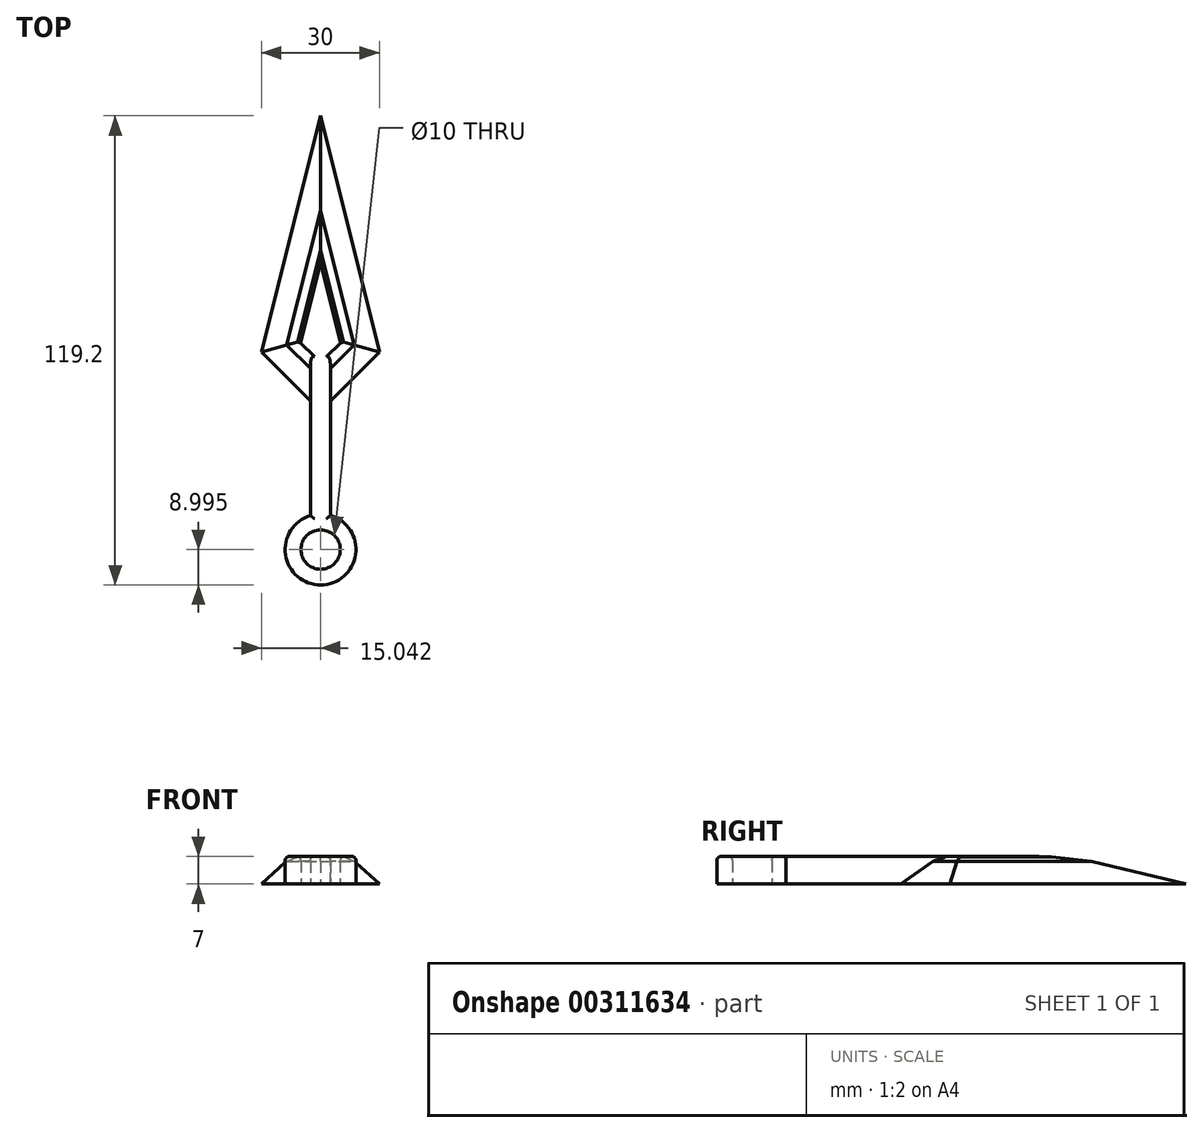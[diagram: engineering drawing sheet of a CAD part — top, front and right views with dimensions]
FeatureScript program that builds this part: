
annotation { "Feature Type Name" : "Feature", "Feature Type Description" : "" }
export const myFeature = defineFeature(function(context is Context, id is Id, definition is map)
    precondition{}
    {
        {
            var Q0;
            Q0=qCreatedBy(makeId("Top.planeOp"),FACE);
            var sketch = newSketch(context, id + "F0", { "sketchPlane" : qUnion([Q0])});
            skLineSegment(sketch, "E0", {"start": v(0, 0) * mm, "end": v(0, 60) * mm, "construction": true});
            skLineSegment(sketch, "E1", {"start": v(0, 0) * mm, "end": v(0, -15) * mm, "construction": true});
            skLineSegment(sketch, "E2", {"start": v(0, -15) * mm, "end": v(0, -45.92) * mm, "construction": true});
            skLineSegment(sketch, "E3", {"start": v(-15, 0) * mm, "end": v(0, 0) * mm, "construction": true});
            skLineSegment(sketch, "E4", {"start": v(0, 0) * mm, "end": v(15, 0) * mm, "construction": true});
            skLineSegment(sketch, "E5", {"start": v(0, 60) * mm, "end": v(-15, 0) * mm});
            skLineSegment(sketch, "E6", {"start": v(-15, 0) * mm, "end": v(0, -15) * mm});
            skLineSegment(sketch, "E7", {"start": v(0, -15) * mm, "end": v(15, 0) * mm});
            skLineSegment(sketch, "E8", {"start": v(15, 0) * mm, "end": v(0, 60) * mm});
            skLineSegment(sketch, "E9", {"start": v(-2.54, -12.46) * mm, "end": v(-2.54, -45.92) * mm});
            skLineSegment(sketch, "E10.MirrorCS", {"start": v(2.54, -12.46) * mm, "end": v(2.54, -45.92) * mm});
            skCircle(sketch, "E11", {"center": v(0.04, -50.2) * mm, "radius": 9 * mm});
            skPoint(sketch, "E11.first.point", {"position": v(0, -59.2) * mm});
            skPoint(sketch, "E11.second.point", {"position": v(0, -41.2) * mm});
            skPoint(sketch, "E11.third.point", {"position": v(8.9, -51.77) * mm});
            skCircle(sketch, "E12", {"center": v(0.04, -50.2) * mm, "radius": 5 * mm});
            skSolve(sketch);
        }
        {
            var Q0;
            {var subQ5=sQuery(id+"F0.wireOp",EDGE,"E5");Q0=makeQuery(id+"F0.imprint","IMPRINT",FACE,{"disambiguationData":[TD([[makeQuery(id+"F0.imprint","IMPRINT",EDGE,{"derivedFrom":subQ5}),1.0]])]});}
            var Q1;
            {var subQ0=sQuery(id+"F0.wireOp",EDGE,"E12");var subQ1=sQuery(id+"F0.wireOp",EDGE,"E9");var subQ2=makeQuery(id+"F0.imprint","INTERSECT",VERTEX,{"derivedFrom":[subQ1,subQ0]});Q1=makeQuery(id+"F0.imprint","IMPRINT",FACE,{"disambiguationData":[TD([[makeQuery(id+"F0.imprint","IMPRINT",EDGE,{"disambiguationData":[TD([[subQ2,1.0]])],"derivedFrom":subQ1}),1.0]])]});}
            var Q2;
            {var subQ0=sQuery(id+"F0.wireOp",EDGE,"E12");var subQ1=sQuery(id+"F0.wireOp",EDGE,"E9");var subQ2=makeQuery(id+"F0.imprint","INTERSECT",VERTEX,{"derivedFrom":[subQ1,subQ0]});Q2=makeQuery(id+"F0.imprint","IMPRINT",FACE,{"disambiguationData":[TD([[makeQuery(id+"F0.imprint","IMPRINT",EDGE,{"disambiguationData":[TD([[subQ2,1.0]])],"derivedFrom":subQ1}),-1.0]])]});}
            var Q3;
            {var subQ1=sQuery(id+"F0.wireOp",EDGE,"E6");var subQ6=sQuery(id+"F0.wireOp",EDGE,"E7");var subQ9=makeQuery(id+"F0.imprint","INTERSECT",VERTEX,{"derivedFrom":[subQ1,subQ6]});Q3=makeQuery(id+"F0.imprint","IMPRINT",FACE,{"disambiguationData":[TD([[makeQuery(id+"F0.imprint","IMPRINT",EDGE,{"disambiguationData":[TD([[subQ9,1.0]])],"derivedFrom":subQ1}),-1.0]])]});}
            extrude(context, id + "F1", {"entities" : qUnion([Q0, Q1, Q2, Q3]), "depth" : 7 * mm});
        }
        {
            var Q0;
            Q0=makeQuery(id+"F1.opExtrude","CAP_EDGE",EDGE,{"disambiguationData":[OSD([sQuery(id+"F0.wireOp",EDGE,"E5")])],"isStart":false});
            var Q1;
            Q1=makeQuery(id+"F1.opExtrude","CAP_EDGE",EDGE,{"disambiguationData":[OSD([sQuery(id+"F0.wireOp",EDGE,"E8")])],"isStart":false});
            var Q2;
            Q2=makeQuery(id+"F1.opExtrude","CAP_EDGE",EDGE,{"disambiguationData":[OSD([sQuery(id+"F0.wireOp",EDGE,"E6")])],"isStart":false});
            var Q3;
            Q3=makeQuery(id+"F1.opExtrude","CAP_EDGE",EDGE,{"disambiguationData":[OSD([sQuery(id+"F0.wireOp",EDGE,"E7")])],"isStart":false});
            chamfer(context, id + "F2", {"entities" : qUnion([Q0, Q1, Q2, Q3]), "width" : 7 * mm, "tangentPropagation" : true});
        }
        {
            var Q0;
            {var subQ0=sQuery(id+"F0.wireOp",EDGE,"E5");Q0=makeQuery(id+"F2.opChamfer","BLEND_EDGE",EDGE,{"blendedFrom":[makeQuery(id+"F1.opExtrude","CAP_EDGE",EDGE,{"disambiguationData":[OSD([subQ0])],"isStart":false}),makeQuery(id+"F1.opExtrude","CAP_FACE",FACE,{"disambiguationData":[OSD([subQ0,sQuery(id+"F0.wireOp",EDGE,"E6"),sQuery(id+"F0.wireOp",EDGE,"E7"),sQuery(id+"F0.wireOp",EDGE,"E8"),sQuery(id+"F0.wireOp",EDGE,"E9"),sQuery(id+"F0.wireOp",EDGE,"E10.MirrorCS"),sQuery(id+"F0.wireOp",EDGE,"E11"),sQuery(id+"F0.wireOp",EDGE,"E12")])],"isStart":false})],"blendedInto":[makeQuery(id+"F1.opExtrude","CAP_FACE",FACE,{"disambiguationData":[OSD([subQ0,sQuery(id+"F0.wireOp",EDGE,"E6"),sQuery(id+"F0.wireOp",EDGE,"E7"),sQuery(id+"F0.wireOp",EDGE,"E8"),sQuery(id+"F0.wireOp",EDGE,"E9"),sQuery(id+"F0.wireOp",EDGE,"E10.MirrorCS"),sQuery(id+"F0.wireOp",EDGE,"E11"),sQuery(id+"F0.wireOp",EDGE,"E12")])],"isStart":false})]});}
            var Q1;
            {var subQ0=sQuery(id+"F0.wireOp",EDGE,"E8");Q1=makeQuery(id+"F2.opChamfer","BLEND_EDGE",EDGE,{"blendedFrom":[makeQuery(id+"F1.opExtrude","CAP_EDGE",EDGE,{"disambiguationData":[OSD([subQ0])],"isStart":false}),makeQuery(id+"F1.opExtrude","CAP_FACE",FACE,{"disambiguationData":[OSD([sQuery(id+"F0.wireOp",EDGE,"E5"),sQuery(id+"F0.wireOp",EDGE,"E6"),sQuery(id+"F0.wireOp",EDGE,"E7"),subQ0,sQuery(id+"F0.wireOp",EDGE,"E9"),sQuery(id+"F0.wireOp",EDGE,"E10.MirrorCS"),sQuery(id+"F0.wireOp",EDGE,"E11"),sQuery(id+"F0.wireOp",EDGE,"E12")])],"isStart":false})],"blendedInto":[makeQuery(id+"F1.opExtrude","CAP_FACE",FACE,{"disambiguationData":[OSD([sQuery(id+"F0.wireOp",EDGE,"E5"),sQuery(id+"F0.wireOp",EDGE,"E6"),sQuery(id+"F0.wireOp",EDGE,"E7"),subQ0,sQuery(id+"F0.wireOp",EDGE,"E9"),sQuery(id+"F0.wireOp",EDGE,"E10.MirrorCS"),sQuery(id+"F0.wireOp",EDGE,"E11"),sQuery(id+"F0.wireOp",EDGE,"E12")])],"isStart":false})]});}
            var Q2;
            {var subQ0=sQuery(id+"F0.wireOp",EDGE,"E6");Q2=makeQuery(id+"F2.opChamfer","BLEND_EDGE",EDGE,{"blendedFrom":[makeQuery(id+"F1.opExtrude","CAP_EDGE",EDGE,{"disambiguationData":[OSD([subQ0])],"isStart":false}),makeQuery(id+"F1.opExtrude","CAP_FACE",FACE,{"disambiguationData":[OSD([sQuery(id+"F0.wireOp",EDGE,"E5"),subQ0,sQuery(id+"F0.wireOp",EDGE,"E7"),sQuery(id+"F0.wireOp",EDGE,"E8"),sQuery(id+"F0.wireOp",EDGE,"E9"),sQuery(id+"F0.wireOp",EDGE,"E10.MirrorCS"),sQuery(id+"F0.wireOp",EDGE,"E11"),sQuery(id+"F0.wireOp",EDGE,"E12")])],"isStart":false})],"blendedInto":[makeQuery(id+"F1.opExtrude","CAP_FACE",FACE,{"disambiguationData":[OSD([sQuery(id+"F0.wireOp",EDGE,"E5"),subQ0,sQuery(id+"F0.wireOp",EDGE,"E7"),sQuery(id+"F0.wireOp",EDGE,"E8"),sQuery(id+"F0.wireOp",EDGE,"E9"),sQuery(id+"F0.wireOp",EDGE,"E10.MirrorCS"),sQuery(id+"F0.wireOp",EDGE,"E11"),sQuery(id+"F0.wireOp",EDGE,"E12")])],"isStart":false})]});}
            var Q3;
            {var subQ0=sQuery(id+"F0.wireOp",EDGE,"E7");Q3=makeQuery(id+"F2.opChamfer","BLEND_EDGE",EDGE,{"blendedFrom":[makeQuery(id+"F1.opExtrude","CAP_EDGE",EDGE,{"disambiguationData":[OSD([subQ0])],"isStart":false}),makeQuery(id+"F1.opExtrude","CAP_FACE",FACE,{"disambiguationData":[OSD([sQuery(id+"F0.wireOp",EDGE,"E5"),sQuery(id+"F0.wireOp",EDGE,"E6"),subQ0,sQuery(id+"F0.wireOp",EDGE,"E8"),sQuery(id+"F0.wireOp",EDGE,"E9"),sQuery(id+"F0.wireOp",EDGE,"E10.MirrorCS"),sQuery(id+"F0.wireOp",EDGE,"E11"),sQuery(id+"F0.wireOp",EDGE,"E12")])],"isStart":false})],"blendedInto":[makeQuery(id+"F1.opExtrude","CAP_FACE",FACE,{"disambiguationData":[OSD([sQuery(id+"F0.wireOp",EDGE,"E5"),sQuery(id+"F0.wireOp",EDGE,"E6"),subQ0,sQuery(id+"F0.wireOp",EDGE,"E8"),sQuery(id+"F0.wireOp",EDGE,"E9"),sQuery(id+"F0.wireOp",EDGE,"E10.MirrorCS"),sQuery(id+"F0.wireOp",EDGE,"E11"),sQuery(id+"F0.wireOp",EDGE,"E12")])],"isStart":false})]});}
            chamfer(context, id + "F3", {"entities" : qUnion([Q0, Q1, Q2, Q3]), "width" : 4 * mm, "tangentPropagation" : true});
        }
        {
            var Q0;
            {var subQ0=sQuery(id+"F0.wireOp",EDGE,"E5");var subQ1=makeQuery(id+"F1.opExtrude","CAP_FACE",FACE,{"disambiguationData":[OSD([subQ0,sQuery(id+"F0.wireOp",EDGE,"E6"),sQuery(id+"F0.wireOp",EDGE,"E7"),sQuery(id+"F0.wireOp",EDGE,"E8"),sQuery(id+"F0.wireOp",EDGE,"E9"),sQuery(id+"F0.wireOp",EDGE,"E10.MirrorCS"),sQuery(id+"F0.wireOp",EDGE,"E11"),sQuery(id+"F0.wireOp",EDGE,"E12")])],"isStart":false});Q0=makeQuery(id+"F3.opChamfer","BLEND_EDGE",EDGE,{"blendedFrom":[makeQuery(id+"F2.opChamfer","BLEND_EDGE",EDGE,{"blendedFrom":[makeQuery(id+"F1.opExtrude","CAP_EDGE",EDGE,{"disambiguationData":[OSD([subQ0])],"isStart":false}),subQ1],"blendedInto":[subQ1]}),subQ1],"blendedInto":[subQ1]});}
            var Q1;
            {var subQ0=sQuery(id+"F0.wireOp",EDGE,"E8");var subQ1=makeQuery(id+"F1.opExtrude","CAP_FACE",FACE,{"disambiguationData":[OSD([sQuery(id+"F0.wireOp",EDGE,"E5"),sQuery(id+"F0.wireOp",EDGE,"E6"),sQuery(id+"F0.wireOp",EDGE,"E7"),subQ0,sQuery(id+"F0.wireOp",EDGE,"E9"),sQuery(id+"F0.wireOp",EDGE,"E10.MirrorCS"),sQuery(id+"F0.wireOp",EDGE,"E11"),sQuery(id+"F0.wireOp",EDGE,"E12")])],"isStart":false});Q1=makeQuery(id+"F3.opChamfer","BLEND_EDGE",EDGE,{"blendedFrom":[makeQuery(id+"F2.opChamfer","BLEND_EDGE",EDGE,{"blendedFrom":[makeQuery(id+"F1.opExtrude","CAP_EDGE",EDGE,{"disambiguationData":[OSD([subQ0])],"isStart":false}),subQ1],"blendedInto":[subQ1]}),subQ1],"blendedInto":[subQ1]});}
            chamfer(context, id + "F4", {"entities" : qUnion([Q0, Q1]), "width" : 2 * mm, "tangentPropagation" : true});
        }
        {
            var Q0;
            Q0=makeQuery(id+"F1.opExtrude","CAP_EDGE",EDGE,{"disambiguationData":[OSD([sQuery(id+"F0.wireOp",EDGE,"E10.MirrorCS")])],"isStart":false});
            var Q1;
            Q1=makeQuery(id+"F1.opExtrude","CAP_EDGE",EDGE,{"disambiguationData":[OSD([sQuery(id+"F0.wireOp",EDGE,"E9")])],"isStart":false});
            var Q2;
            Q2=makeQuery(id+"F1.opExtrude","CAP_EDGE",EDGE,{"disambiguationData":[OSD([sQuery(id+"F0.wireOp",EDGE,"E11")])],"isStart":false});
            var Q3;
            Q3=makeQuery(id+"F1.opExtrude","CAP_EDGE",EDGE,{"disambiguationData":[OSD([sQuery(id+"F0.wireOp",EDGE,"E12")])],"isStart":false});
            fillet(context, id + "F5", {"entities" : qUnion([Q0, Q1, Q2, Q3]), "radius" : 1 * mm, "tangentPropagation" : true, "allowEdgeOverflow" : false});
        }
    });
